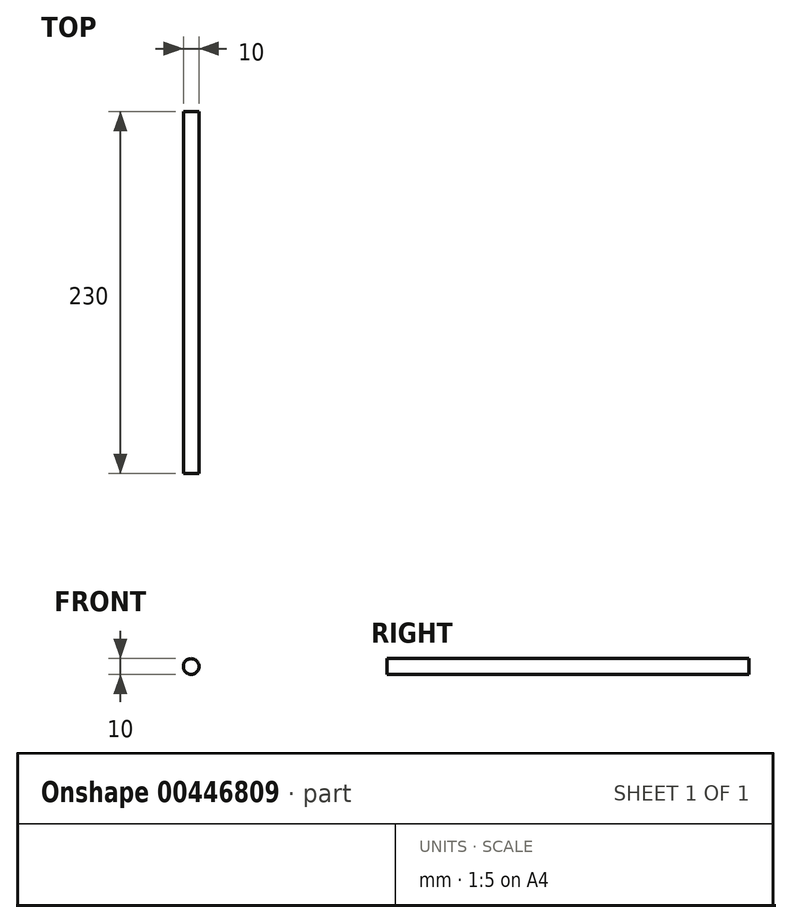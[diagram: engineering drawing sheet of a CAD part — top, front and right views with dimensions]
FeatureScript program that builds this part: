
annotation { "Feature Type Name" : "Feature", "Feature Type Description" : "" }
export const myFeature = defineFeature(function(context is Context, id is Id, definition is map)
    precondition{}
    {
        {
            var Q0;
            Q0=qCreatedBy(makeId("Front.planeOp"),FACE);
            var sketch = newSketch(context, id + "F0", { "sketchPlane" : qUnion([Q0])});
            skCircle(sketch, "E0", {"center": v(0, 0) * mm, "radius": 5 * mm});
            skSolve(sketch);
        }
        {
            var Q0;
            Q0=qSketchRegion(id+"F0",true);
            extrude(context, id + "F1", {"entities" : qUnion([Q0]), "endBound" : BoundingType.SYMMETRIC, "depth" : 230 * mm});
        }
    });
